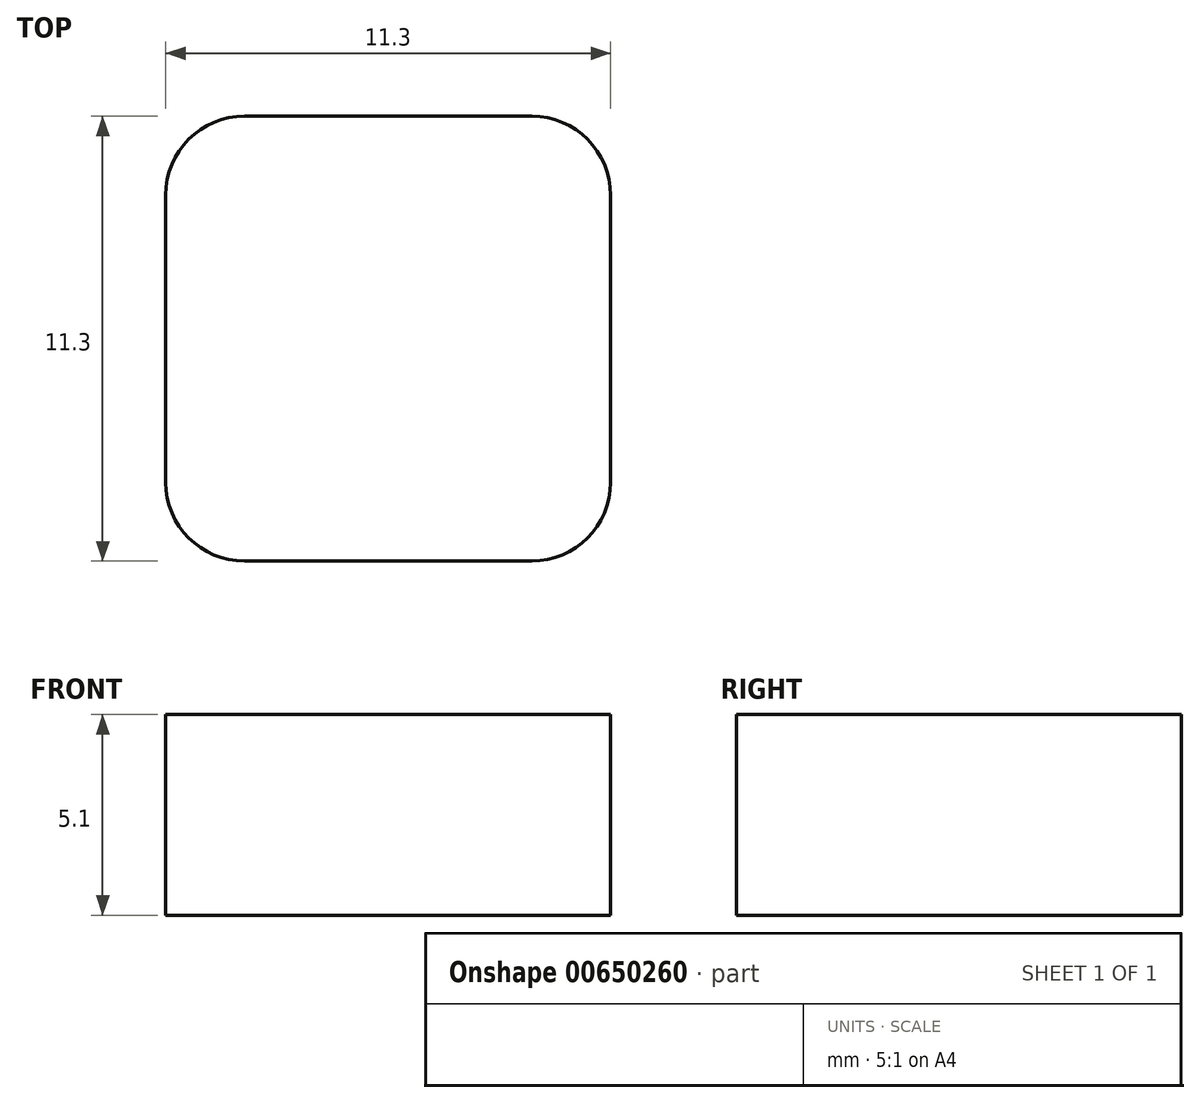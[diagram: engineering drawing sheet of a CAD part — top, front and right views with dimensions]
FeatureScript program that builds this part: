
annotation { "Feature Type Name" : "Feature", "Feature Type Description" : "" }
export const myFeature = defineFeature(function(context is Context, id is Id, definition is map)
    precondition{}
    {
        {
            var Q0;
            Q0=qCreatedBy(makeId("Top.planeOp"),FACE);
            var sketch = newSketch(context, id + "F0", { "sketchPlane" : qUnion([Q0])});
            skLineSegment(sketch, "E0.bottom", {"start": v(0, 0) * mm, "end": v(11.3, 0) * mm});
            skLineSegment(sketch, "E0.top", {"start": v(0, 11.3) * mm, "end": v(11.3, 11.3) * mm});
            skLineSegment(sketch, "E0.left", {"start": v(0, 0) * mm, "end": v(0, 11.3) * mm});
            skLineSegment(sketch, "E0.right", {"start": v(11.3, 0) * mm, "end": v(11.3, 11.3) * mm});
            skSolve(sketch);
        }
        {
            var Q0;
            Q0=makeQuery(id+"F0.imprint","IMPRINT",FACE,{"disambiguationData":[TD([[makeQuery(id+"F0.imprint","IMPRINT",EDGE,{"derivedFrom":sQuery(id+"F0.wireOp",EDGE,"E0.bottom")}),1.0]])]});
            extrude(context, id + "F1", {"entities" : qUnion([Q0]), "depth" : 16.4 * mm, "offsetDistance" : 25 * mm});
        }
        {
            var Q0;
            Q0=makeQuery(id+"F1.opExtrude","SWEPT_FACE",FACE,{"disambiguationData":[OSD([sQuery(id+"F0.wireOp",EDGE,"E0.left")])]});
            var sketch = newSketch(context, id + "F2", { "sketchPlane" : qUnion([Q0])});
            skLineSegment(sketch, "E1.bottom", {"start": v(0, 0) * mm, "end": v(-11.3, 0) * mm});
            skLineSegment(sketch, "E1.top", {"start": v(0, 11.3) * mm, "end": v(-11.3, 11.3) * mm});
            skLineSegment(sketch, "E1.left", {"start": v(0, 0) * mm, "end": v(0, 11.3) * mm});
            skLineSegment(sketch, "E1.right", {"start": v(-11.3, 0) * mm, "end": v(-11.3, 11.3) * mm});
            skSolve(sketch);
        }
        {
            var Q0;
            Q0=makeQuery(id+"F2.imprint","IMPRINT",FACE,{"disambiguationData":[TD([[makeQuery(id+"F2.imprint","IMPRINT",EDGE,{"derivedFrom":sQuery(id+"F2.wireOp",EDGE,"E1.bottom")}),-1.0]])]});
            extrude(context, id + "F3", {"entities" : qUnion([Q0]), "operationType" : NewBodyOperationType.REMOVE, "oppositeDirection" : true, "depth" : 25 * mm, "offsetDistance" : 25 * mm});
        }
        {
            var Q0;
            Q0=makeQuery(id+"F1.opExtrude","SWEPT_EDGE",EDGE,{"disambiguationData":[OSD([sQuery(id+"F0.wireOp",EDGE,"E0.bottom"),sQuery(id+"F0.wireOp",EDGE,"E0.left")])]});
            var Q1;
            Q1=makeQuery(id+"F1.opExtrude","SWEPT_EDGE",EDGE,{"disambiguationData":[OSD([sQuery(id+"F0.wireOp",EDGE,"E0.bottom"),sQuery(id+"F0.wireOp",EDGE,"E0.right")])]});
            var Q2;
            Q2=makeQuery(id+"F1.opExtrude","SWEPT_EDGE",EDGE,{"disambiguationData":[OSD([sQuery(id+"F0.wireOp",EDGE,"E0.top"),sQuery(id+"F0.wireOp",EDGE,"E0.left")])]});
            var Q3;
            Q3=makeQuery(id+"F1.opExtrude","SWEPT_EDGE",EDGE,{"disambiguationData":[OSD([sQuery(id+"F0.wireOp",EDGE,"E0.top"),sQuery(id+"F0.wireOp",EDGE,"E0.right")])]});
            fillet(context, id + "F4", {"entities" : qUnion([Q0, Q1, Q2, Q3]), "radius" : 2 * mm, "tangentPropagation" : true, "allowEdgeOverflow" : false});
        }
    });
